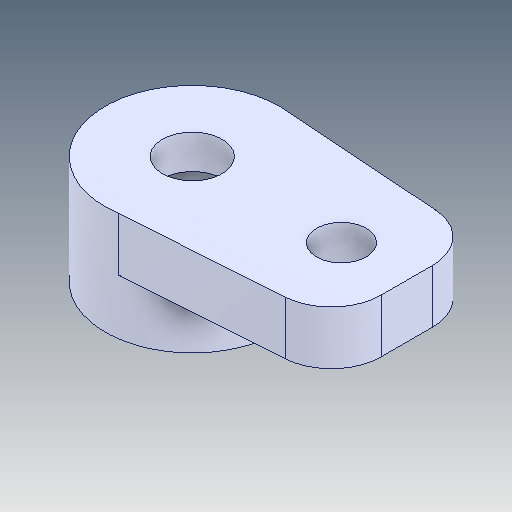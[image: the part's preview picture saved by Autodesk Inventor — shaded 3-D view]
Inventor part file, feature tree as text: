
AUTODESK INVENTOR PART (.ipt)
format: ipt  version: 2020 (Build 240168000, 168)  size: 118,272 bytes
history: mixed  units: mm
features: fillet x1, imported_body x1
ambient origin geometry x8: Origin, YZ Plane, XZ Plane, XY Plane, X Axis, Y Axis, Z Axis, Center Point
bodies: Solid1 (imported_parasolid)
feature tree (2):
  fillet  "Fillet1"  [1 undecoded]
  imported_body  NMx_Import_Brep_tag  [imported B-rep: ~13 faces, bbox_mm=[8.624907, 4.37, 6.966093]]
note: 1 required parameter value undecoded (feature->parameter linkage not recoverable at this tier; creation-order binding heuristic only, values carry confidence <= 0.55)
